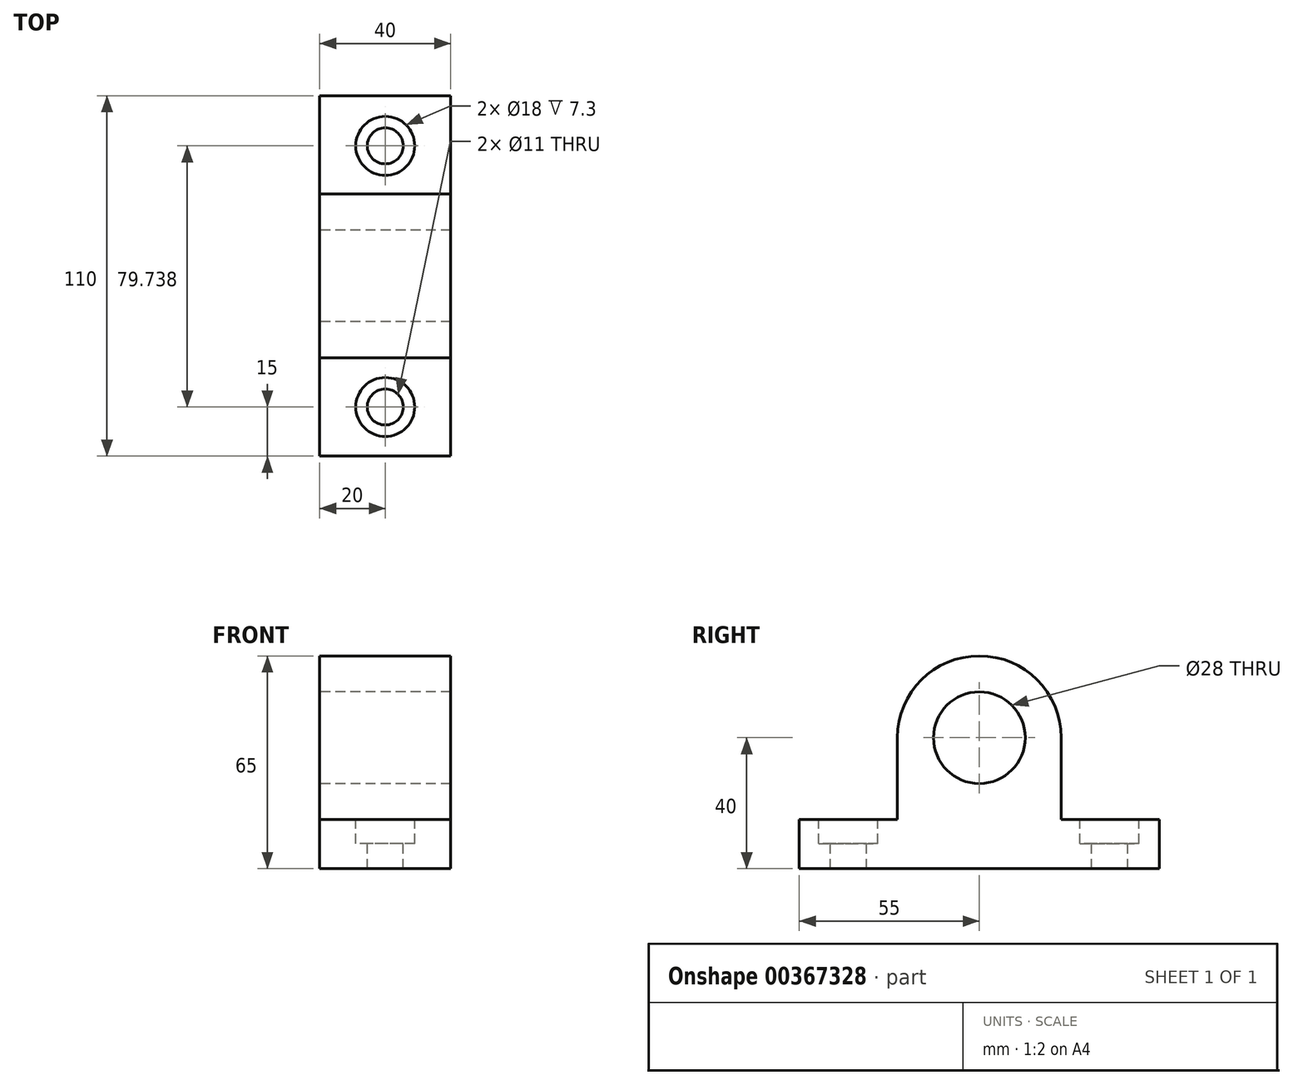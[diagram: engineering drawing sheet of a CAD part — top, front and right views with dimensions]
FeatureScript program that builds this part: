
annotation { "Feature Type Name" : "Feature", "Feature Type Description" : "" }
export const myFeature = defineFeature(function(context is Context, id is Id, definition is map)
    precondition{}
    {
        {
            var Q0;
            Q0=qCreatedBy(makeId("Right.planeOp"),FACE);
            var sketch = newSketch(context, id + "F0", { "sketchPlane" : qUnion([Q0])});
            skLineSegment(sketch, "E0", {"start": v(0, 0) * mm, "end": v(30, 0) * mm});
            skLineSegment(sketch, "E1", {"start": v(30, 0) * mm, "end": v(30, -15) * mm});
            skLineSegment(sketch, "E2", {"start": v(30, -15) * mm, "end": v(-80, -15) * mm});
            skLineSegment(sketch, "E3", {"start": v(-80, -15) * mm, "end": v(-80, 0) * mm});
            skLineSegment(sketch, "E4", {"start": v(-80, 0) * mm, "end": v(-50, 0) * mm});
            skLineSegment(sketch, "E5", {"start": v(0, 0) * mm, "end": v(0, 25) * mm});
            skLineSegment(sketch, "E6", {"start": v(-50, 25) * mm, "end": v(-50, 0) * mm});
            skArc(sketch, "E7", {"start": v(0, 25) * mm, "mid": v(-25, 50) * mm, "end": v(-50, 25) * mm});
            skCircle(sketch, "E8", {"center": v(-25, 25) * mm, "radius": 14 * mm});
            skLineSegment(sketch, "E9", {"start": v(-74, 0) * mm, "end": v(-74, -7.3) * mm});
            skLineSegment(sketch, "E10", {"start": v(-74, -7.3) * mm, "end": v(-56, -7.3) * mm});
            skLineSegment(sketch, "E11", {"start": v(-56, -7.3) * mm, "end": v(-56, 0) * mm});
            skLineSegment(sketch, "E12", {"start": v(-59.5, -7.3) * mm, "end": v(-59.5, -15) * mm});
            skLineSegment(sketch, "E13", {"start": v(-70.5, -15) * mm, "end": v(-70.5, -7.3) * mm});
            skLineSegment(sketch, "E14", {"start": v(6, 0) * mm, "end": v(6, -7.3) * mm});
            skLineSegment(sketch, "E15", {"start": v(6, -7.3) * mm, "end": v(24, -7.3) * mm});
            skLineSegment(sketch, "E16", {"start": v(24, -7.3) * mm, "end": v(24, 0) * mm});
            skLineSegment(sketch, "E17", {"start": v(9.5, -7.3) * mm, "end": v(9.5, -15) * mm});
            skLineSegment(sketch, "E18", {"start": v(20.5, -7.3) * mm, "end": v(20.5, -15) * mm});
            skSolve(sketch);
        }
        {
            var Q0;
            Q0 = qSketchRegion(id + "F0", true);
            extrude(context, id + "F1", {"entities" : qUnion([Q0]), "depth" : 40 * mm});
        }
        {
            var Q0;
            Q0=makeQuery(id+"F1.opExtrude","SWEPT_FACE",FACE,{"disambiguationData":[OSD([sQuery(id+"F0.wireOp",EDGE,"E4")])]});
            var sketch = newSketch(context, id + "F2", { "sketchPlane" : qUnion([Q0])});
            skCircle(sketch, "E19", {"center": v(20, -65) * mm, "radius": 5.5 * mm});
            skCircle(sketch, "E20", {"center": v(20, -65) * mm, "radius": 9 * mm});
            skLineSegment(sketch, "E21", {"start": v(20, 29.48) * mm, "end": v(20, 0) * mm});
            skPoint(sketch, "E21.startSnap0", {"position": v(20, -80) * mm});
            skLineSegment(sketch, "E22", {"start": v(20, 14.74) * mm, "end": v(0, 14.74) * mm});
            skLineSegment(sketch, "E23", {"start": v(20, 14.74) * mm, "end": v(40, 14.74) * mm});
            skCircle(sketch, "E24", {"center": v(20, 14.74) * mm, "radius": 5.5 * mm});
            skCircle(sketch, "E25", {"center": v(20, 14.74) * mm, "radius": 9 * mm});
            skSolve(sketch);
        }
        {
            var Q0;
            Q0 = qSketchRegion(id + "F2", true);
            extrude(context, id + "F3", {"entities" : qUnion([Q0]), "operationType" : NewBodyOperationType.REMOVE, "oppositeDirection" : true, "depth" : 7.3 * mm});
        }
        {
            var Q0;
            Q0=makeQuery(id+"F3.boolean.opBoolean","SPLIT",FACE,{"disambiguationData":[TD([makeQuery(id+"F3.opExtrude","SWEPT_FACE",FACE,{"disambiguationData":[OSD([sQuery(id+"F2.wireOp",EDGE,"E24")])]})])],"derivedFrom":makeQuery(id+"F1.opExtrude","SWEPT_FACE",FACE,{"disambiguationData":[OSD([sQuery(id+"F0.wireOp",EDGE,"E0")])]})});
            var Q1;
            Q1=makeQuery(id+"F3.boolean.opBoolean","SPLIT",FACE,{"disambiguationData":[TD([makeQuery(id+"F3.opExtrude","SWEPT_FACE",FACE,{"disambiguationData":[OSD([sQuery(id+"F2.wireOp",EDGE,"E19")])]})])],"derivedFrom":makeQuery(id+"F1.opExtrude","SWEPT_FACE",FACE,{"disambiguationData":[OSD([sQuery(id+"F0.wireOp",EDGE,"E4")])]})});
            extrude(context, id + "F4", {"entities" : qUnion([Q0, Q1]), "operationType" : NewBodyOperationType.REMOVE, "oppositeDirection" : true, "depth" : 15 * mm});
        }
    });
